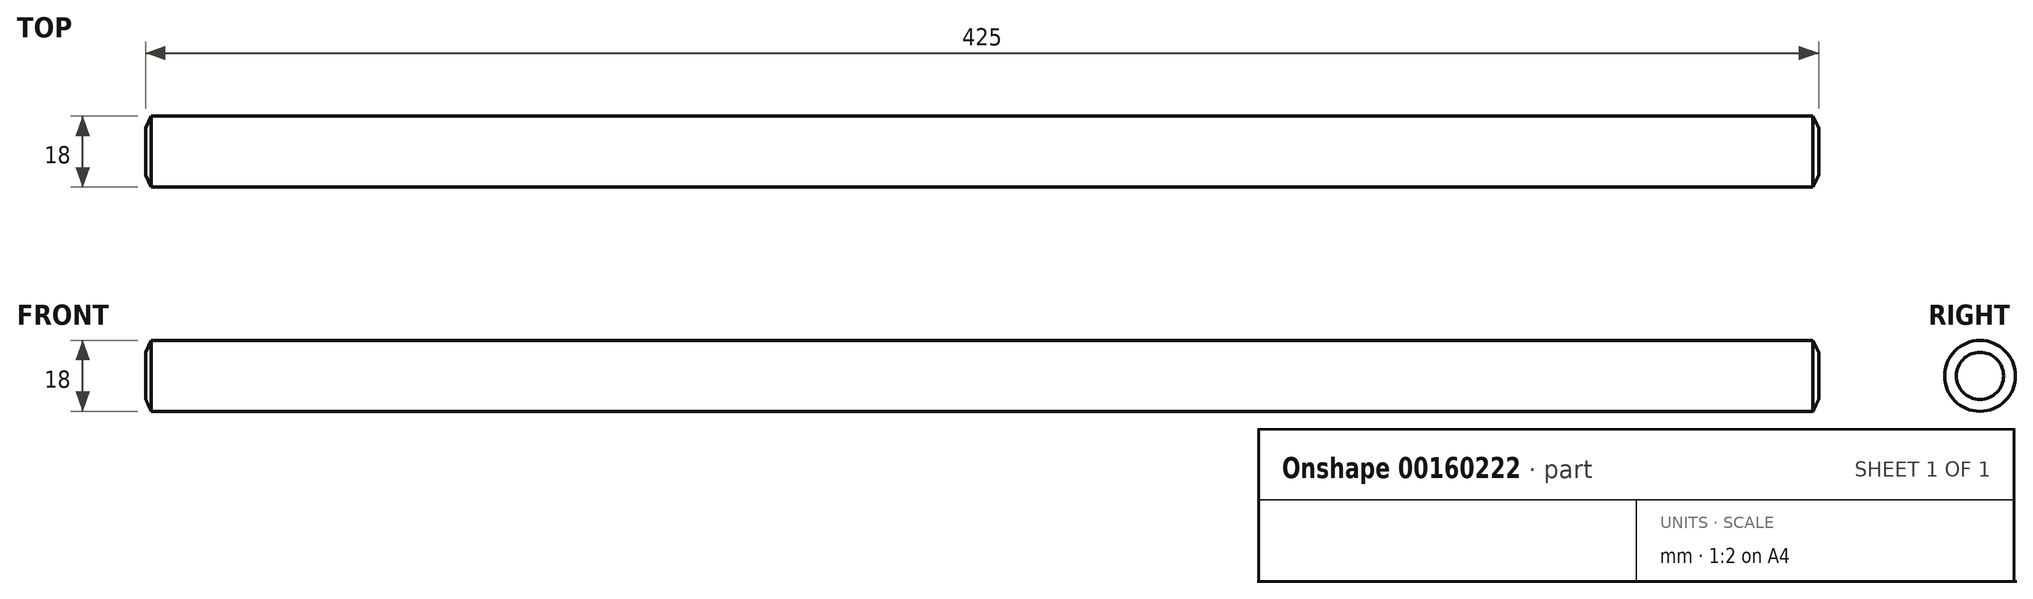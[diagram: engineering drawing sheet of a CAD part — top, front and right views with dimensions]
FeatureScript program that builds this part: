
annotation { "Feature Type Name" : "Feature", "Feature Type Description" : "" }
export const myFeature = defineFeature(function(context is Context, id is Id, definition is map)
    precondition{}
    {
        {
            var Q0;
            Q0=qCreatedBy(makeId("Right.planeOp"),FACE);
            var sketch = newSketch(context, id + "F0", { "sketchPlane" : qUnion([Q0])});
            skCircle(sketch, "E0", {"center": v(0, 0) * mm, "radius": 9 * mm});
            skSolve(sketch);
        }
        {
            var Q0;
            Q0=makeQuery(id+"F0.imprint","IMPRINT",FACE,{"disambiguationData":[TD([[makeQuery(id+"F0.imprint","IMPRINT",EDGE,{"derivedFrom":sQuery(id+"F0.wireOp",EDGE,"E0")}),1.0]])]});
            extrude(context, id + "F1", {"entities" : qUnion([Q0]), "depth" : 425 * mm});
        }
        {
            var Q0;
            Q0=makeQuery(id+"F1.opExtrude","CAP_EDGE",EDGE,{"disambiguationData":[OSD([sQuery(id+"F0.wireOp",EDGE,"E0")])],"isStart":false});
            var Q1;
            Q1=makeQuery(id+"F1.opExtrude","CAP_EDGE",EDGE,{"disambiguationData":[OSD([sQuery(id+"F0.wireOp",EDGE,"E0")])],"isStart":true});
            chamfer(context, id + "F2", {"entities" : qUnion([Q0, Q1]), "chamferType" : ChamferType.OFFSET_ANGLE, "width" : 3 * mm, "oppositeDirection" : false, "angle" : 25 * degree, "tangentPropagation" : true});
        }
    });
